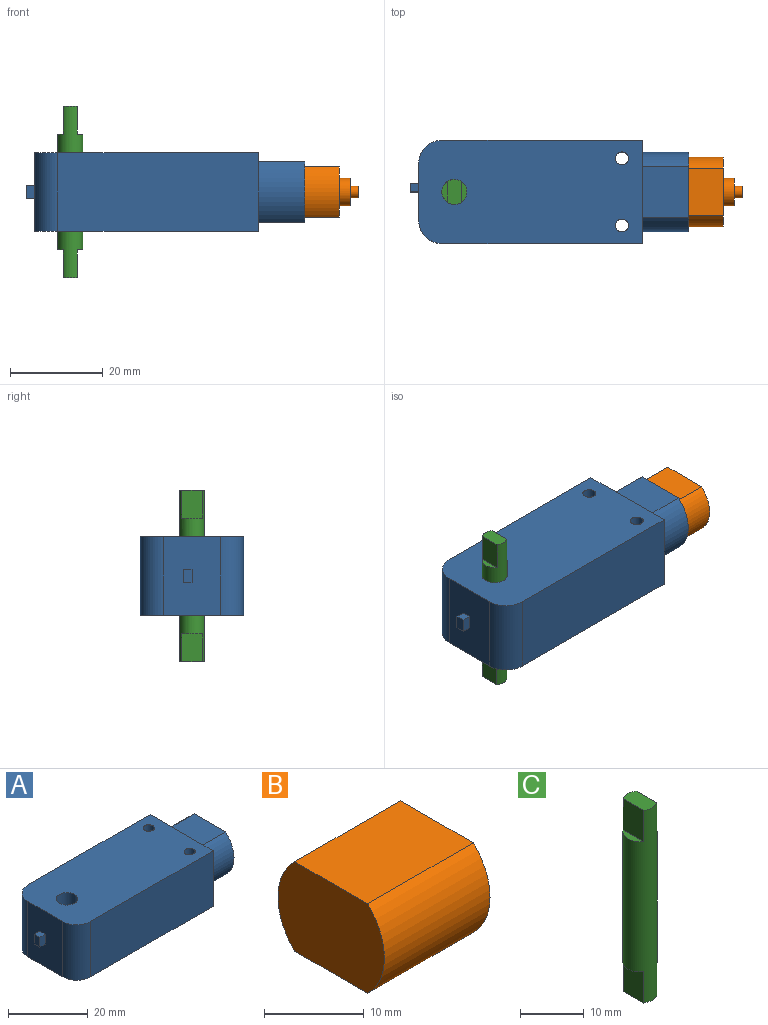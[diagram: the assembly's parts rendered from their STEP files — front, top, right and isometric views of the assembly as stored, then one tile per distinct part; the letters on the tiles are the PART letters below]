
ASSEMBLY  parts=3 mates=2
PART A: 36 faces, bbox 60.2x22.3x17 mm
  f0: plane 17.1x13mm, normal (1,0,0), area 48.5mm2, adj f17,f18,f19,f20,f32,f33,f34,f35
  f1: plane 22.3x17mm, normal (1,0,0), area 180.6mm2, adj f2,f6,f10,f11,f17,f18,f19,f20
  f2: plane 43.3x17mm, normal (0,1,0), area 736.1mm2, adj f1,f3,f10,f11
  f3: cylinder r=5mm len=17mm, axis (0,0,-1), area 133.5mm2, adj f2,f4,f10,f11
  f4: plane 17x12.3mm, normal (-1,0,0), area 203.5mm2, adj f3,f5,f10,f11,f12,f13,f15,f16
  f5: cylinder r=5mm len=17mm, axis (0,0,-1), area 133.5mm2, adj f4,f6,f10,f11
  f6: plane 43.3x17mm, normal (0,-1,0), area 736.1mm2, adj f1,f5,f10,f11
  f7: cylinder r=1.4mm len=17mm, axis (0,0,-1), area 149.5mm2, adj f10,f11
  f8: cylinder r=1.4mm len=17mm, axis (0,0,-1), area 149.5mm2, adj f10,f11
  f9: cylinder r=2.7mm len=17mm, axis (0,0,-1), area 288.4mm2, adj f10,f11
  f10: plane 48.3x22.3mm, normal (0,0,1), area 1031.1mm2, adj f1,f2,f3,f4,f5,f6,f7,f8
  f11: plane 48.3x22.3mm, normal (0,0,-1), area 1031.1mm2, adj f1,f2,f3,f4,f5,f6,f7,f8
  f12: plane 3x1.88mm, normal (0,-1,0), area 5.6mm2, adj f4,f14,f15,f16
  f13: plane 3x1.88mm, normal (0,1,0), area 5.6mm2, adj f4,f14,f15,f16
  f14: plane 3x1.88mm, normal (-1,0,0), area 5.6mm2, adj f12,f13,f15,f16
  f15: plane 1.88x1.88mm, normal (0,0,1), area 3.5mm2, adj f4,f12,f13,f14
  f16: plane 1.88x1.88mm, normal (0,0,-1), area 3.5mm2, adj f4,f12,f13,f14
  f17: plane 11.11x10mm, normal (0,0,-1), area 111.1mm2, adj f0,f1,f18,f20
  f18: cylinder r=8.55mm len=13mm, axis (-1,0,0), area 147.7mm2, adj f0,f1,f17,f19
  f19: plane 11.11x10mm, normal (0,0,1), area 111.1mm2, adj f0,f1,f18,f20
  f20: cylinder r=8.55mm len=13mm, axis (-1,0,0), area 147.7mm2, adj f0,f1,f17,f19
  f21: plane 20.3x15mm, normal (-1,0,0), area 154.6mm2, adj f22,f26,f30,f31,f32,f33,f34,f35
  f22: plane 42.3x15mm, normal (0,-1,0), area 634.5mm2, adj f21,f23,f30,f31
  f23: cylinder r=4mm len=15mm, axis (0,0,-1), area 94.2mm2, adj f22,f24,f30,f31
  f24: plane 15x12.3mm, normal (1,0,0), area 184.5mm2, adj f23,f25,f30,f31
  f25: cylinder r=4mm len=15mm, axis (0,0,-1), area 94.2mm2, adj f24,f26,f30,f31
  f26: plane 42.3x15mm, normal (0,1,0), area 634.5mm2, adj f21,f25,f30,f31
  f27: cylinder r=2.4mm len=15mm, axis (0,0,-1), area 226.2mm2, adj f30,f31
  f28: cylinder r=2.4mm len=15mm, axis (0,0,-1), area 226.2mm2, adj f30,f31
  f29: cylinder r=3.7mm len=15mm, axis (0,0,-1), area 348.7mm2, adj f30,f31
  f30: plane 46.3x20.3mm, normal (0,0,-1), area 853.8mm2, adj f21,f22,f23,f24,f25,f26,f27,f28
  f31: plane 46.3x20.3mm, normal (0,0,1), area 853.8mm2, adj f21,f22,f23,f24,f25,f26,f27,f28
  f32: plane 11x10.34mm, normal (0,0,1), area 113.8mm2, adj f0,f21,f33,f35
  f33: cylinder r=7.55mm len=11mm, axis (-1,0,0), area 135.6mm2, adj f0,f21,f32,f34
  f34: plane 11x10.34mm, normal (0,0,-1), area 113.8mm2, adj f0,f21,f33,f35
  f35: cylinder r=7.55mm len=11mm, axis (-1,0,0), area 135.6mm2, adj f0,f21,f32,f34
PART B: 10 faces, bbox 19x15.1x11 mm
  f0: plane 15x10.34mm, normal (0,0,-1), area 155.2mm2, adj f1,f3,f4,f5
  f1: cylinder r=7.55mm len=15mm, axis (-1,0,0), area 184.8mm2, adj f0,f2,f4,f5
  f2: plane 15x10.34mm, normal (0,0,1), area 155.2mm2, adj f1,f3,f4,f5
  f3: cylinder r=7.55mm len=15mm, axis (-1,0,0), area 184.8mm2, adj f0,f2,f4,f5
  f4: plane 15.1x11mm, normal (1,0,0), area 121.7mm2, adj f0,f1,f2,f3,f6
  f5: plane 15.1x11mm, normal (-1,0,0), area 149.9mm2, adj f0,f1,f2,f3
  f6: cylinder r=3mm len=6mm, axis (-1,0,0), area 43.4mm2, adj f4,f7
  f7: plane 6x6mm, normal (1,0,0), area 23.4mm2, adj f6,f8
  f8: cylinder r=1.25mm len=2.5mm, axis (-1,0,0), area 13.4mm2, adj f7,f9
  f9: plane 2.5x2.5mm, normal (1,0,0), area 4.9mm2, adj f8
PART C: 11 faces, bbox 5.4x5.4x37 mm
  f0: plane 5.4x3.05mm, normal (0,0,-1), area 15.6mm2, adj f2,f7,f9
  f1: plane 5.4x2.98mm, normal (0,0,1), area 15.2mm2, adj f2,f3,f5
  f2: cylinder r=2.7mm len=37mm, axis (0,0,-1), area 500.9mm2, adj f0,f1,f3,f4,f5,f6,f7,f8
  f3: plane 6x4.5mm, normal (1,0,0), area 27mm2, adj f1,f2,f4
  f4: plane 4.5x1.21mm, normal (0,0,1), area 3.8mm2, adj f2,f3
  f5: plane 6x4.5mm, normal (-1,0,0), area 27mm2, adj f1,f2,f6
  f6: plane 4.5x1.21mm, normal (0,0,1), area 3.8mm2, adj f2,f5
  f7: plane 6x4.45mm, normal (1,0,0), area 26.7mm2, adj f0,f2,f8
  f8: plane 4.45x1.17mm, normal (0,0,-1), area 3.7mm2, adj f2,f7
  f9: plane 6x4.45mm, normal (-1,0,0), area 26.7mm2, adj f0,f2,f10
  f10: plane 4.45x1.17mm, normal (0,0,-1), area 3.7mm2, adj f2,f9
PLACE A t=(12.36,4.33,-0.18)mm
PLACE B t=(4.86,4.33,-0.18)mm
PLACE C t=(12.36,4.33,-0.18)mm
MATE fastened B.f1 <-> A.f18  axis (-1,0,0) through (46.51,4.33,-0.18)mm
MATE revolute C.f2 <-> A.f9  axis (0,0,-1) through (-4.09,4.33,-0.18)mm
